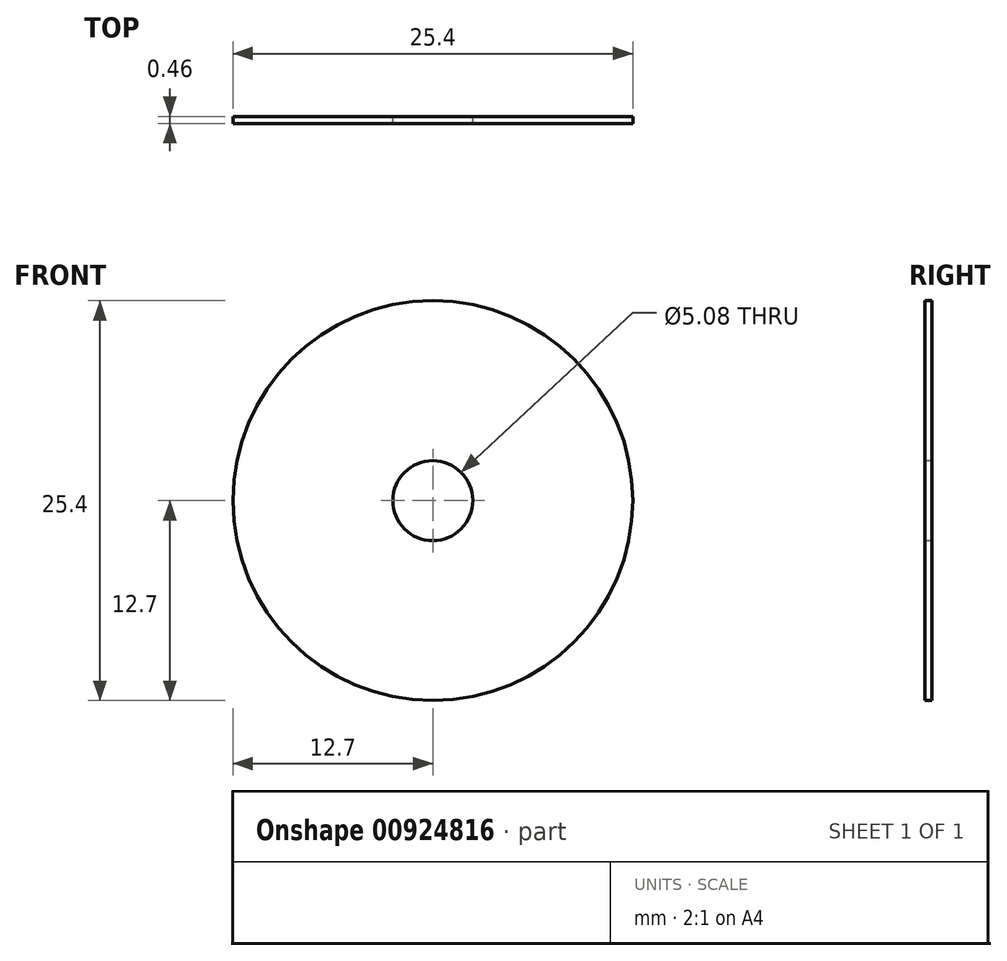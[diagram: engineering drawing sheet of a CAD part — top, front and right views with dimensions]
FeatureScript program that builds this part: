
annotation { "Feature Type Name" : "Feature", "Feature Type Description" : "" }
export const myFeature = defineFeature(function(context is Context, id is Id, definition is map)
    precondition{}
    {
        {
            var Q0;
            Q0=qCreatedBy(makeId("Front.planeOp"),FACE);
            var sketch = newSketch(context, id + "F0", { "sketchPlane" : qUnion([Q0])});
            skCircle(sketch, "E0", {"center": v(0, 0) * mm, "radius": 2.54 * mm});
            skCircle(sketch, "E1", {"center": v(0, 0) * mm, "radius": 12.7 * mm});
            skSolve(sketch);
        }
        {
            var Q0;
            Q0=makeQuery(id+"F0.imprint","IMPRINT",FACE,{"disambiguationData":[TD([[makeQuery(id+"F0.imprint","IMPRINT",EDGE,{"derivedFrom":sQuery(id+"F0.wireOp",EDGE,"E0")}),-1.0]])]});
            extrude(context, id + "F1", {"entities" : qUnion([Q0]), "depth" : 0.46 * mm, "offsetDistance" : 25.4 * mm});
        }
    });
